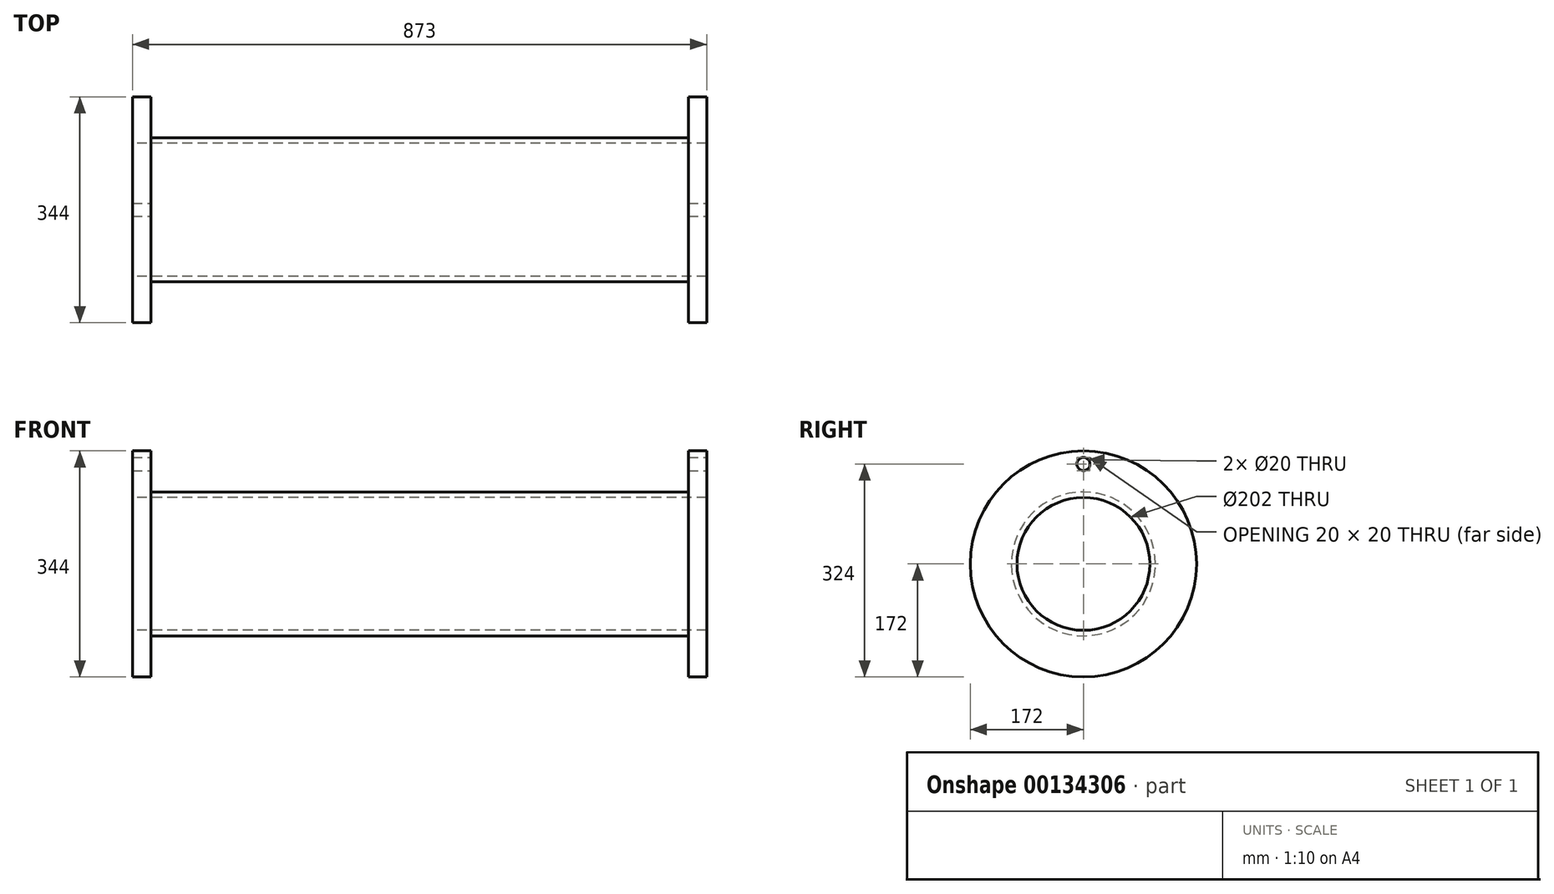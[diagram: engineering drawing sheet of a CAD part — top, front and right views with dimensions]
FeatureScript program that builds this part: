
annotation { "Feature Type Name" : "Feature", "Feature Type Description" : "" }
export const myFeature = defineFeature(function(context is Context, id is Id, definition is map)
    precondition{}
    {
        {
            var Q0;
            Q0=qCreatedBy(makeId("Front.planeOp"),FACE);
            var sketch = newSketch(context, id + "F0", { "sketchPlane" : qUnion([Q0])});
            skLineSegment(sketch, "E0.bottom", {"start": v(0, 109.5) * mm, "end": v(408.5, 109.5) * mm});
            skLineSegment(sketch, "E0.top", {"start": v(0, 101) * mm, "end": v(436.5, 101) * mm});
            skLineSegment(sketch, "E0.left", {"start": v(0, 109.5) * mm, "end": v(0, 101) * mm});
            skLineSegment(sketch, "E1.bottom", {"start": v(408.5, 172) * mm, "end": v(436.5, 172) * mm});
            skLineSegment(sketch, "E1.right", {"start": v(436.5, 172) * mm, "end": v(436.5, 101) * mm});
            skLineSegment(sketch, "E2", {"start": v(408.5, 109.5) * mm, "end": v(408.5, 172) * mm});
            skLineSegment(sketch, "E3", {"start": v(0, 0) * mm, "end": v(150.96, 0) * mm, "construction": true});
            skSolve(sketch);
        }
        {
            var Q0;
            Q0=makeQuery(id+"F0.imprint","IMPRINT",FACE,{"disambiguationData":[TD([[makeQuery(id+"F0.imprint","IMPRINT",EDGE,{"derivedFrom":sQuery(id+"F0.wireOp",EDGE,"E0.bottom")}),-1.0]])]});
            var Q1;
            Q1=sQuery(id+"F0.wireOp",EDGE,"E3");
            revolve(context, id + "F1", {"entities" : qUnion([Q0]), "axis" : qUnion([Q1]), "revolveType" : RevolveType.FULL});
        }
        {
            var Q0;
            Q0=makeQuery(id+"F1.opRevolve","SWEPT_BODY",BODY,{"disambiguationData":[OSD([sQuery(id+"F0.wireOp",EDGE,"E0.bottom"),sQuery(id+"F0.wireOp",EDGE,"E0.top"),sQuery(id+"F0.wireOp",EDGE,"E0.left"),sQuery(id+"F0.wireOp",EDGE,"E1.bottom"),sQuery(id+"F0.wireOp",EDGE,"E1.right"),sQuery(id+"F0.wireOp",EDGE,"E2")])]});
            var Q1;
            Q1=qCreatedBy(makeId("Right.planeOp"),FACE);
            mirror(context, id + "F2", {"operationType" : NewBodyOperationType.ADD, "entities" : qUnion([Q0]), "mirrorPlane" : qUnion([Q1])});
        }
        {
            var Q0;
            Q0=makeQuery(id+"F1.opRevolve","SWEPT_FACE",FACE,{"disambiguationData":[OSD([sQuery(id+"F0.wireOp",EDGE,"E1.right")])]});
            var sketch = newSketch(context, id + "F3", { "sketchPlane" : qUnion([Q0])});
            skCircle(sketch, "E4", {"center": v(0, 152) * mm, "radius": 10 * mm});
            skSolve(sketch);
        }
        {
            var Q0;
            Q0=makeQuery(id+"F3.imprint","IMPRINT",FACE,{"disambiguationData":[TD([[makeQuery(id+"F3.imprint","IMPRINT",EDGE,{"derivedFrom":sQuery(id+"F3.wireOp",EDGE,"E4")}),1.0]])]});
            extrude(context, id + "F4", {"entities" : qUnion([Q0]), "operationType" : NewBodyOperationType.REMOVE, "endBound" : BoundingType.THROUGH_ALL, "oppositeDirection" : true, "depth" : 25 * mm});
        }
    });
